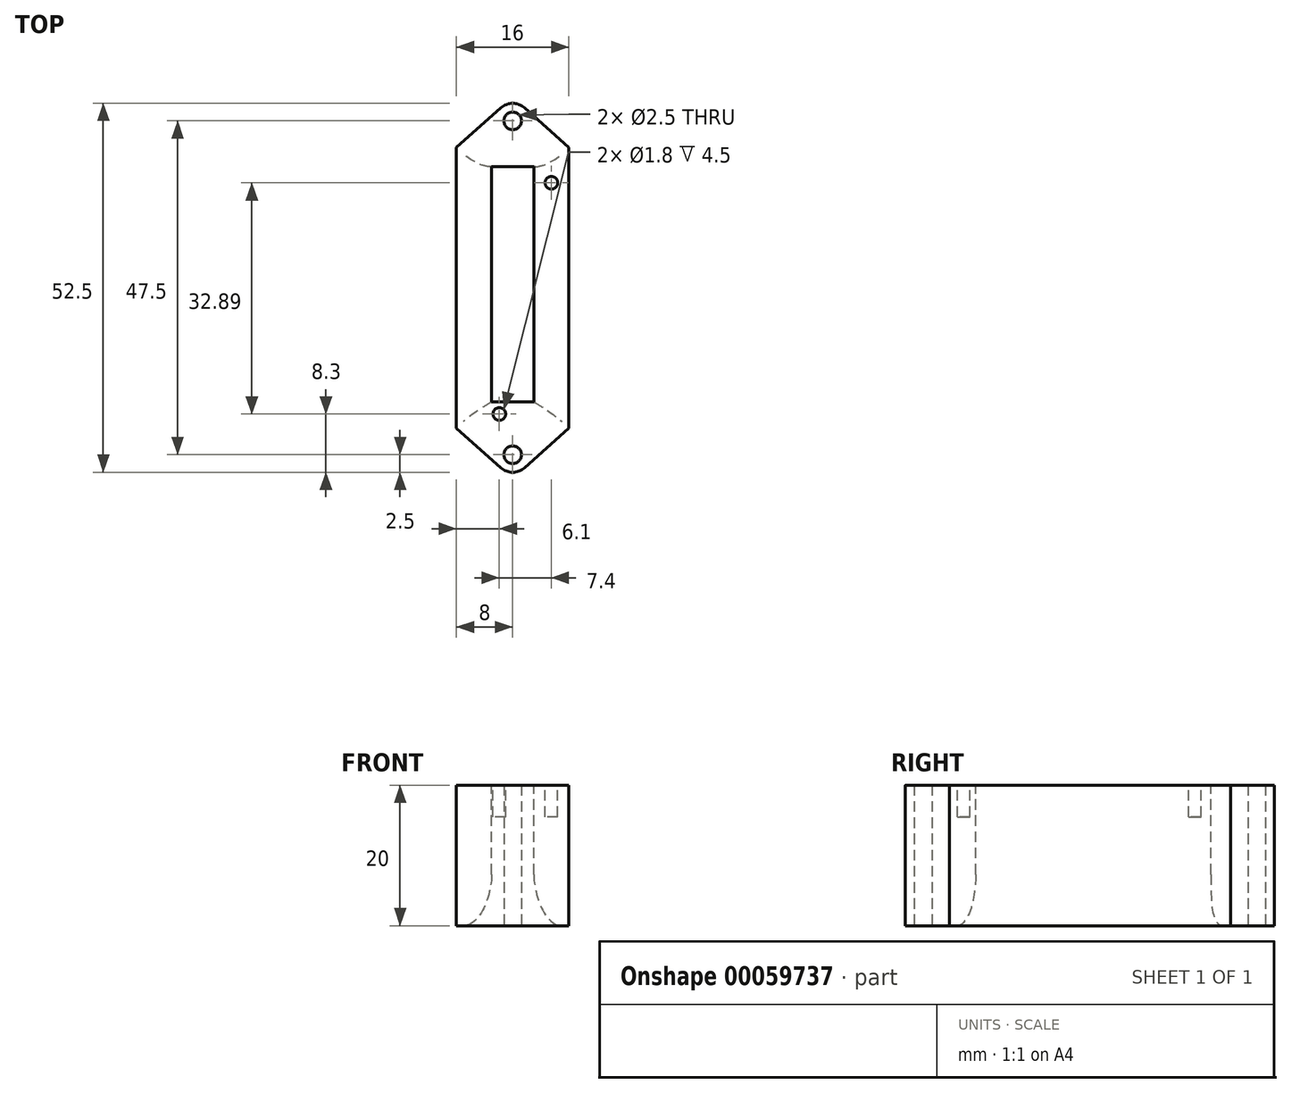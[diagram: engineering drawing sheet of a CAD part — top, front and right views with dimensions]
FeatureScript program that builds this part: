
annotation { "Feature Type Name" : "Feature", "Feature Type Description" : "" }
export const myFeature = defineFeature(function(context is Context, id is Id, definition is map)
    precondition{}
    {
        {
            var Q0;
            Q0=qCreatedBy(makeId("Top.planeOp"),FACE);
            var sketch = newSketch(context, id + "F0", { "sketchPlane" : qUnion([Q0])});
            skLineSegment(sketch, "E0", {"start": v(-8, 20) * mm, "end": v(-1.66, 25.62) * mm});
            skLineSegment(sketch, "E1", {"start": v(-8, 20) * mm, "end": v(-8, 0) * mm});
            skLineSegment(sketch, "E2.MirrorCS", {"start": v(8, 20) * mm, "end": v(8, 0) * mm});
            skLineSegment(sketch, "E3.MirrorCS", {"start": v(8, 20) * mm, "end": v(1.66, 25.62) * mm});
            skLineSegment(sketch, "E4.MirrorCS", {"start": v(-8, -20) * mm, "end": v(-8, 0) * mm});
            skLineSegment(sketch, "E5.MirrorCS", {"start": v(8, -20) * mm, "end": v(8, 0) * mm});
            skLineSegment(sketch, "E6.MirrorCS", {"start": v(-8, -20) * mm, "end": v(-1.66, -25.62) * mm});
            skLineSegment(sketch, "E7.MirrorCS", {"start": v(8, -20) * mm, "end": v(1.66, -25.62) * mm});
            skCircle(sketch, "E8", {"center": v(0, 23.75) * mm, "radius": 2.5 * mm});
            skCircle(sketch, "E9.MirrorC", {"center": v(0, -23.75) * mm, "radius": 2.5 * mm});
            skLineSegment(sketch, "E10", {"start": v(0, 23.75) * mm, "end": v(0, 26.25) * mm, "construction": true});
            skCircle(sketch, "E11.0", {"center": v(0, 23.75) * mm, "radius": 1.25 * mm});
            skLineSegment(sketch, "E12", {"start": v(-8, 20) * mm, "end": v(8, 20) * mm});
            skLineSegment(sketch, "E13.MirrorCS", {"start": v(-8, -20) * mm, "end": v(8, -20) * mm});
            skLineSegment(sketch, "E14.0", {"start": v(-7, 19) * mm, "end": v(-7, 0) * mm});
            skLineSegment(sketch, "E14.1", {"start": v(7, 19) * mm, "end": v(7, 0) * mm});
            skLineSegment(sketch, "E14.2", {"start": v(7, -19) * mm, "end": v(7, 0) * mm});
            skLineSegment(sketch, "E14.3", {"start": v(-7, 19) * mm, "end": v(7, 19) * mm});
            skLineSegment(sketch, "E14.4", {"start": v(-7, -19) * mm, "end": v(7, -19) * mm});
            skLineSegment(sketch, "E14.5", {"start": v(-7, -19) * mm, "end": v(-7, 0) * mm});
            skCircle(sketch, "E15.MirrorC", {"center": v(0, -23.75) * mm, "radius": 1.25 * mm});
            skSolve(sketch);
        }
        {
            var Q0;
            Q0 = qSketchRegion(id + "F0", true);
            extrude(context, id + "F1", {"entities" : qUnion([Q0]), "depth" : 20 * mm});
        }
        {
            var Q0;
            Q0=makeQuery(id+"F1.opExtrude","CAP_FACE",FACE,{"disambiguationData":[OSD([sQuery(id+"F0.wireOp",EDGE,"E1"),sQuery(id+"F0.wireOp",EDGE,"E3.MirrorCS"),sQuery(id+"F0.wireOp",EDGE,"E0"),sQuery(id+"F0.wireOp",EDGE,"E2.MirrorCS"),sQuery(id+"F0.wireOp",EDGE,"E6.MirrorCS"),sQuery(id+"F0.wireOp",EDGE,"E4.MirrorCS"),sQuery(id+"F0.wireOp",EDGE,"E7.MirrorCS"),sQuery(id+"F0.wireOp",EDGE,"E5.MirrorCS"),sQuery(id+"F0.wireOp",EDGE,"E8"),sQuery(id+"F0.wireOp",EDGE,"E9.MirrorC"),sQuery(id+"F0.wireOp",EDGE,"E11.0"),sQuery(id+"F0.wireOp",EDGE,"E14.0"),sQuery(id+"F0.wireOp",EDGE,"E14.1"),sQuery(id+"F0.wireOp",EDGE,"E14.2"),sQuery(id+"F0.wireOp",EDGE,"E14.3"),sQuery(id+"F0.wireOp",EDGE,"E14.4"),sQuery(id+"F0.wireOp",EDGE,"E14.5"),sQuery(id+"F0.wireOp",EDGE,"E15.MirrorC")])],"isStart":false});
            var sketch = newSketch(context, id + "F2", { "sketchPlane" : qUnion([Q0])});
            skLineSegment(sketch, "E16.bottom", {"start": v(3, 17.25) * mm, "end": v(-3, 17.25) * mm});
            skLineSegment(sketch, "E16.top", {"start": v(3, -16.25) * mm, "end": v(-3, -16.25) * mm});
            skLineSegment(sketch, "E16.left", {"start": v(3, 17.25) * mm, "end": v(3, -16.25) * mm});
            skLineSegment(sketch, "E16.right", {"start": v(-3, 17.25) * mm, "end": v(-3, -16.25) * mm});
            skPoint(sketch, "E16.middle", {"position": v(0, 0) * mm});
            skLineSegment(sketch, "E17.bottom", {"start": v(-7, 19) * mm, "end": v(7, 19) * mm});
            skLineSegment(sketch, "E17.top", {"start": v(-7, -19) * mm, "end": v(7, -19) * mm});
            skLineSegment(sketch, "E17.left", {"start": v(-7, 19) * mm, "end": v(-7, -19) * mm});
            skLineSegment(sketch, "E17.right", {"start": v(7, 19) * mm, "end": v(7, -19) * mm});
            skSolve(sketch);
        }
        {
            var Q0;
            Q0 = qSketchRegion(id + "F2", true);
            extrude(context, id + "F3", {"entities" : qUnion([Q0]), "operationType" : NewBodyOperationType.ADD, "oppositeDirection" : true, "depth" : 12.7 * mm});
        }
        {
            var Q0;
            Q0=makeQuery(id+"F1.opExtrude","SWEPT_FACE",FACE,{"disambiguationData":[OSD([sQuery(id+"F0.wireOp",EDGE,"E14.0"),sQuery(id+"F0.wireOp",EDGE,"E14.5")])]});
            var sketch = newSketch(context, id + "F4", { "sketchPlane" : qUnion([Q0])});
            skFitSpline(sketch, "E18", {"points": [v(-19, 0) * mm, v(-16.25, 7.3) * mm], "startDerivative": vector(6.1, 0) * mm, "endDerivative": vector(0, 7.6) * mm});
            skLineSegment(sketch, "E19", {"start": v(-16.25, 7.3) * mm, "end": v(-19, 7.3) * mm});
            skLineSegment(sketch, "E20", {"start": v(-19, 7.3) * mm, "end": v(-19, 0) * mm});
            skLineSegment(sketch, "E21.MirrorCS", {"start": v(17.25, 7.3) * mm, "end": v(19, 7.3) * mm});
            skLineSegment(sketch, "E22.MirrorCS", {"start": v(19, 7.3) * mm, "end": v(19, 0) * mm});
            skFitSpline(sketch, "E23.MirrorCS", {"points": [v(19, 0) * mm, v(17.25, 7.3) * mm], "startDerivative": vector(-6.1, 0) * mm, "endDerivative": vector(0, 7.6) * mm});
            skSolve(sketch);
        }
        {
            var Q0;
            Q0=makeQuery(id+"F1.opExtrude","SWEPT_FACE",FACE,{"disambiguationData":[OSD([sQuery(id+"F0.wireOp",EDGE,"E14.4")])]});
            var sketch = newSketch(context, id + "F5", { "sketchPlane" : qUnion([Q0])});
            skLineSegment(sketch, "E24", {"start": v(7, 0) * mm, "end": v(7, 7.3) * mm});
            skLineSegment(sketch, "E25", {"start": v(7, 7.3) * mm, "end": v(3, 7.3) * mm});
            skFitSpline(sketch, "E26", {"points": [v(7, 0) * mm, v(3, 7.3) * mm], "startDerivative": vector(-7.41, 0) * mm, "endDerivative": vector(0, 8.17) * mm});
            skFitSpline(sketch, "E27.MirrorCS", {"points": [v(-7, 0) * mm, v(-3, 7.3) * mm], "startDerivative": vector(7.41, 0) * mm, "endDerivative": vector(0, 8.17) * mm});
            skLineSegment(sketch, "E28.MirrorCS", {"start": v(-7, 7.3) * mm, "end": v(-3, 7.3) * mm});
            skLineSegment(sketch, "E29.MirrorCS", {"start": v(-7, 0) * mm, "end": v(-7, 7.3) * mm});
            skSolve(sketch);
        }
        {
            var Q0;
            Q0 = qSketchRegion(id + "F4", true);
            var Q1;
            Q1=makeQuery(id+"F1.opExtrude","CAP_EDGE",EDGE,{"disambiguationData":[OSD([sQuery(id+"F0.wireOp",EDGE,"E14.3")])],"isStart":true});
            sweep(context, id + "F6", {"operationType" : NewBodyOperationType.ADD, "profiles" : qUnion([Q0]), "path" : qUnion([Q1])});
        }
        {
            var Q0;
            Q0 = qSketchRegion(id + "F5", true);
            var Q1;
            Q1=makeQuery(id+"F1.opExtrude","CAP_EDGE",EDGE,{"disambiguationData":[OSD([sQuery(id+"F0.wireOp",EDGE,"E14.0"),sQuery(id+"F0.wireOp",EDGE,"E14.5")])],"isStart":true});
            sweep(context, id + "F7", {"operationType" : NewBodyOperationType.ADD, "profiles" : qUnion([Q0]), "path" : qUnion([Q1])});
        }
        {
            var Q0;
            Q0=makeQuery(id+"F3.boolean.opBoolean","MERGE",FACE,{"derivedFrom":[makeQuery(id+"F1.opExtrude","CAP_FACE",FACE,{"disambiguationData":[OSD([sQuery(id+"F0.wireOp",EDGE,"E1"),sQuery(id+"F0.wireOp",EDGE,"E3.MirrorCS"),sQuery(id+"F0.wireOp",EDGE,"E0"),sQuery(id+"F0.wireOp",EDGE,"E2.MirrorCS"),sQuery(id+"F0.wireOp",EDGE,"E6.MirrorCS"),sQuery(id+"F0.wireOp",EDGE,"E4.MirrorCS"),sQuery(id+"F0.wireOp",EDGE,"E7.MirrorCS"),sQuery(id+"F0.wireOp",EDGE,"E5.MirrorCS"),sQuery(id+"F0.wireOp",EDGE,"E8"),sQuery(id+"F0.wireOp",EDGE,"E9.MirrorC"),sQuery(id+"F0.wireOp",EDGE,"E11.0"),sQuery(id+"F0.wireOp",EDGE,"E14.0"),sQuery(id+"F0.wireOp",EDGE,"E14.1"),sQuery(id+"F0.wireOp",EDGE,"E14.2"),sQuery(id+"F0.wireOp",EDGE,"E14.3"),sQuery(id+"F0.wireOp",EDGE,"E14.4"),sQuery(id+"F0.wireOp",EDGE,"E14.5"),sQuery(id+"F0.wireOp",EDGE,"E15.MirrorC")])],"isStart":false}),makeQuery(id+"F3.opExtrude","CAP_FACE",FACE,{"disambiguationData":[OSD([sQuery(id+"F2.wireOp",EDGE,"E16.bottom"),sQuery(id+"F2.wireOp",EDGE,"E16.top"),sQuery(id+"F2.wireOp",EDGE,"E16.left"),sQuery(id+"F2.wireOp",EDGE,"E16.right"),sQuery(id+"F2.wireOp",EDGE,"E17.bottom"),sQuery(id+"F2.wireOp",EDGE,"E17.top"),sQuery(id+"F2.wireOp",EDGE,"E17.left"),sQuery(id+"F2.wireOp",EDGE,"E17.right")])],"isStart":true})]});
            var sketch = newSketch(context, id + "F8", { "sketchPlane" : qUnion([Q0])});
            skCircle(sketch, "E30", {"center": v(-5.5, 14.94) * mm, "radius": 0.85 * mm, "construction": true});
            skCircle(sketch, "E31", {"center": v(1.9, -17.95) * mm, "radius": 0.85 * mm, "construction": true});
            skCircle(sketch, "E32.0", {"center": v(-5.5, 14.94) * mm, "radius": 0.9 * mm, "construction": true});
            skCircle(sketch, "E33.0", {"center": v(1.9, -17.95) * mm, "radius": 0.9 * mm, "construction": true});
            skCircle(sketch, "E34.0", {"center": v(0, -23.75) * mm, "radius": 1.25 * mm, "construction": true});
            skCircle(sketch, "E35.0", {"center": v(0, 23.75) * mm, "radius": 1.25 * mm, "construction": true});
            skCircle(sketch, "E36.MirrorC", {"center": v(5.5, 14.94) * mm, "radius": 0.9 * mm});
            skCircle(sketch, "E37.MirrorC", {"center": v(-1.9, -17.95) * mm, "radius": 0.9 * mm});
            skCircle(sketch, "E38", {"center": v(1.27, -14.75) * mm, "radius": 0.45 * mm, "construction": true});
            skCircle(sketch, "E39.0.1.0", {"center": v(1.27, -12.21) * mm, "radius": 0.45 * mm, "construction": true});
            skCircle(sketch, "E39.0.2.0", {"center": v(1.27, -9.67) * mm, "radius": 0.45 * mm, "construction": true});
            skCircle(sketch, "E39.0.3.0", {"center": v(1.27, -7.13) * mm, "radius": 0.45 * mm, "construction": true});
            skCircle(sketch, "E39.0.4.0", {"center": v(1.27, -4.6) * mm, "radius": 0.45 * mm, "construction": true});
            skCircle(sketch, "E39.0.5.0", {"center": v(1.27, -2.05) * mm, "radius": 0.45 * mm, "construction": true});
            skCircle(sketch, "E39.0.6.0", {"center": v(1.27, 0.49) * mm, "radius": 0.45 * mm, "construction": true});
            skCircle(sketch, "E39.0.7.0", {"center": v(1.27, 3.03) * mm, "radius": 0.45 * mm, "construction": true});
            skCircle(sketch, "E39.0.8.0", {"center": v(1.27, 5.57) * mm, "radius": 0.45 * mm, "construction": true});
            skCircle(sketch, "E39.0.9.0", {"center": v(1.27, 8.1) * mm, "radius": 0.45 * mm, "construction": true});
            skCircle(sketch, "E39.0.10.0", {"center": v(1.27, 10.65) * mm, "radius": 0.45 * mm, "construction": true});
            skCircle(sketch, "E39.0.11.0", {"center": v(1.27, 13.2) * mm, "radius": 0.45 * mm, "construction": true});
            skCircle(sketch, "E39.0.12.0", {"center": v(1.27, 15.73) * mm, "radius": 0.45 * mm, "construction": true});
            skLineSegment(sketch, "E39.direction1", {"start": v(1.27, -14.75) * mm, "end": v(-1.27, -14.75) * mm, "construction": true});
            skLineSegment(sketch, "E39.direction2", {"start": v(1.27, -14.75) * mm, "end": v(1.27, -12.21) * mm, "construction": true});
            skCircle(sketch, "E40.0.1.0", {"center": v(-1.27, -14.75) * mm, "radius": 0.45 * mm, "construction": true});
            skCircle(sketch, "E40.0.1.1", {"center": v(-1.27, -12.21) * mm, "radius": 0.45 * mm, "construction": true});
            skCircle(sketch, "E40.0.1.2", {"center": v(-1.27, -9.67) * mm, "radius": 0.45 * mm, "construction": true});
            skCircle(sketch, "E40.0.1.3", {"center": v(-1.27, -7.13) * mm, "radius": 0.45 * mm, "construction": true});
            skCircle(sketch, "E40.0.1.4", {"center": v(-1.27, -4.6) * mm, "radius": 0.45 * mm, "construction": true});
            skCircle(sketch, "E40.0.1.5", {"center": v(-1.27, -2.05) * mm, "radius": 0.45 * mm, "construction": true});
            skCircle(sketch, "E40.0.1.6", {"center": v(-1.27, 0.49) * mm, "radius": 0.45 * mm, "construction": true});
            skCircle(sketch, "E40.0.1.7", {"center": v(-1.27, 3.03) * mm, "radius": 0.45 * mm, "construction": true});
            skCircle(sketch, "E40.0.1.8", {"center": v(-1.27, 5.57) * mm, "radius": 0.45 * mm, "construction": true});
            skCircle(sketch, "E40.0.1.9", {"center": v(-1.27, 8.1) * mm, "radius": 0.45 * mm, "construction": true});
            skCircle(sketch, "E40.0.1.10", {"center": v(-1.27, 10.65) * mm, "radius": 0.45 * mm, "construction": true});
            skCircle(sketch, "E40.0.1.11", {"center": v(-1.27, 13.2) * mm, "radius": 0.45 * mm, "construction": true});
            skCircle(sketch, "E40.0.1.12", {"center": v(-1.27, 15.73) * mm, "radius": 0.45 * mm, "construction": true});
            skSolve(sketch);
        }
        {
            var Q0;
            Q0 = qSketchRegion(id + "F8", true);
            extrude(context, id + "F9", {"entities" : qUnion([Q0]), "operationType" : NewBodyOperationType.REMOVE, "oppositeDirection" : true, "depth" : 4.5 * mm});
        }
    });
